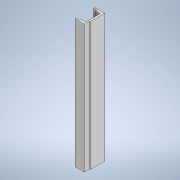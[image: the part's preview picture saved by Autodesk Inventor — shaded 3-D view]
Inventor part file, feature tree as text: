
AUTODESK INVENTOR PART (.ipt)
format: ipt  version: 2020.1 (Build 241239000, 239)  size: 115,200 bytes
history: native  units: mm
features: other x1, extrude x1, sketch x1
ambient origin geometry x8: Origin, YZ Plane, XZ Plane, XY Plane, X Axis, Y Axis, Z Axis, Center Point
bodies: Body1 (feature_tree)
feature tree (3):
  other  "Твердое тело1"
  extrude  "Выдавливание1"  Depth=120.0mm
  sketch  "Эскиз1"
